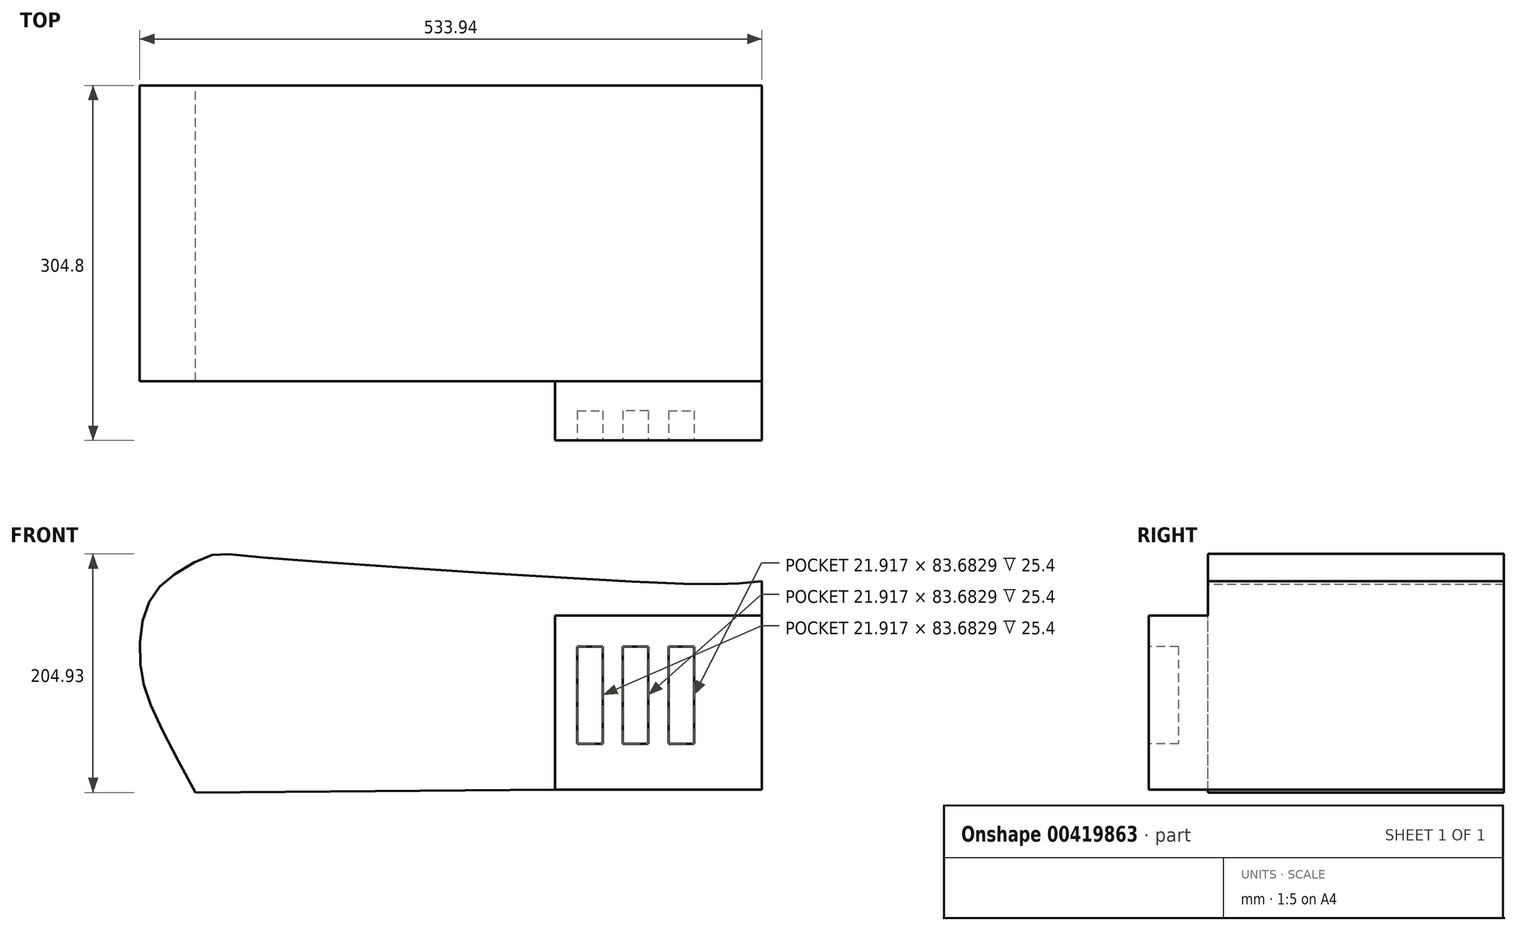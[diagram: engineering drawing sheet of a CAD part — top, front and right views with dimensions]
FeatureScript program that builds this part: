
annotation { "Feature Type Name" : "Feature", "Feature Type Description" : "" }
export const myFeature = defineFeature(function(context is Context, id is Id, definition is map)
    precondition{}
    {
        {
            var Q0;
            Q0=qCreatedBy(makeId("Front.planeOp"),FACE);
            var sketch = newSketch(context, id + "F0", { "sketchPlane" : qUnion([Q0])});
            skLineSegment(sketch, "E0.bottom", {"start": v(85.88, -146.83) * mm, "end": v(263.47, -146.83) * mm});
            skLineSegment(sketch, "E0.top", {"start": v(85.88, 2.72) * mm, "end": v(263.47, 2.72) * mm});
            skLineSegment(sketch, "E0.left", {"start": v(85.88, -146.83) * mm, "end": v(85.88, 2.72) * mm});
            skLineSegment(sketch, "E0.right", {"start": v(263.47, -146.83) * mm, "end": v(263.47, 2.72) * mm});
            skFitSpline(sketch, "E1", {"points": [v(-222.57, -149.17) * mm, v(-259.96, -76.73) * mm, v(-269.3, -44.02) * mm, v(-269.3, -8.96) * mm, v(-259.96, 19.08) * mm, v(-241.26, 37.77) * mm, v(-210.89, 54.13) * mm, v(-180.5, 54.13) * mm, v(179.35, 30.76) * mm, v(247.1, 30.76) * mm, v(286.83, 35.43) * mm, v(314.87, 40.1) * mm], "startDerivative": vector(-395.83, 720.92) * mm, "endDerivative": vector(404.96, 72.08) * mm});
            skLineSegment(sketch, "E2", {"start": v(-222.57, -149.17) * mm, "end": v(85.88, -146.83) * mm});
            skLineSegment(sketch, "E3", {"start": v(263.47, 2.72) * mm, "end": v(263.47, 32.4) * mm});
            skSolve(sketch);
        }
        {
            var Q0;
            Q0=makeQuery(id+"F0.imprint","IMPRINT",FACE,{"disambiguationData":[TD([[makeQuery(id+"F0.imprint","IMPRINT",EDGE,{"derivedFrom":sQuery(id+"F0.wireOp",EDGE,"E0.bottom")}),1.0]])]});
            extrude(context, id + "F1", {"entities" : qUnion([Q0]), "depth" : 304.8 * mm});
        }
        {
            var Q0;
            Q0 = qSketchRegion(id + "F0", true);
            extrude(context, id + "F2", {"entities" : qUnion([Q0]), "operationType" : NewBodyOperationType.ADD, "depth" : 254 * mm});
        }
        {
            var Q0;
            Q0=makeQuery(id+"F1.opExtrude","CAP_FACE",FACE,{"disambiguationData":[OSD([sQuery(id+"F0.wireOp",EDGE,"E0.bottom"),sQuery(id+"F0.wireOp",EDGE,"E0.top"),sQuery(id+"F0.wireOp",EDGE,"E0.left"),sQuery(id+"F0.wireOp",EDGE,"E0.right")])],"isStart":false});
            var sketch = newSketch(context, id + "F3", { "sketchPlane" : qUnion([Q0])});
            skLineSegment(sketch, "E4.bottom", {"start": v(105.11, -23.73) * mm, "end": v(127.03, -23.73) * mm});
            skLineSegment(sketch, "E4.top", {"start": v(105.11, -107.4) * mm, "end": v(127.03, -107.4) * mm});
            skLineSegment(sketch, "E4.left", {"start": v(105.11, -23.73) * mm, "end": v(105.11, -107.4) * mm});
            skLineSegment(sketch, "E4.right", {"start": v(127.03, -23.73) * mm, "end": v(127.03, -107.4) * mm});
            skLineSegment(sketch, "E5.MirrorCS", {"start": v(144.1, -23.73) * mm, "end": v(144.1, -107.4) * mm});
            skLineSegment(sketch, "E6.MirrorCS", {"start": v(166.02, -23.73) * mm, "end": v(166.02, -107.4) * mm});
            skLineSegment(sketch, "E7.MirrorCS", {"start": v(166.02, -23.73) * mm, "end": v(144.1, -23.73) * mm});
            skLineSegment(sketch, "E8.MirrorCS", {"start": v(166.02, -107.4) * mm, "end": v(144.1, -107.4) * mm});
            skPoint(sketch, "E9.startSnap0", {"position": v(174.67, 2.72) * mm});
            skPoint(sketch, "E9.endSnap0", {"position": v(174.67, -146.83) * mm});
            skLineSegment(sketch, "E10.MirrorCS", {"start": v(183.32, -23.73) * mm, "end": v(183.32, -107.4) * mm});
            skLineSegment(sketch, "E11.MirrorCS", {"start": v(205.24, -23.73) * mm, "end": v(205.24, -107.4) * mm});
            skLineSegment(sketch, "E12.MirrorCS", {"start": v(183.32, -23.73) * mm, "end": v(205.24, -23.73) * mm});
            skLineSegment(sketch, "E13.MirrorCS", {"start": v(183.32, -107.4) * mm, "end": v(205.24, -107.4) * mm});
            skPoint(sketch, "E14.orphan", {"position": v(174.67, 56.11) * mm});
            skPoint(sketch, "E9.end.orphan", {"position": v(174.67, -167.04) * mm});
            skLineSegment(sketch, "E15", {"start": v(85.88, -14.48) * mm, "end": v(-270.9, -14.48) * mm});
            skLineSegment(sketch, "E16", {"start": v(85.88, -72.06) * mm, "end": v(-260.65, -72.06) * mm});
            skLineSegment(sketch, "E17", {"start": v(-208.27, -148.82) * mm, "end": v(-208.27, 53.84) * mm});
            skLineSegment(sketch, "E18", {"start": v(-126.3, -146.55) * mm, "end": v(-126.3, 51.56) * mm});
            skLineSegment(sketch, "E19.MirrorCS", {"start": v(-44.32, -148.82) * mm, "end": v(-44.32, 53.84) * mm});
            skLineSegment(sketch, "E20.MirrorCS", {"start": v(37.65, -146.55) * mm, "end": v(37.65, 51.56) * mm});
            skLineSegment(sketch, "E21", {"start": v(121.9, 2.72) * mm, "end": v(121.9, 36.76) * mm});
            skLineSegment(sketch, "E22", {"start": v(194.77, 2.72) * mm, "end": v(194.77, 31.07) * mm});
            skFitSpline(sketch, "E23.0", {"points": [v(-228.14, -152.22) * mm, v(-231.8, -145.55) * mm, v(-239.14, -132.18) * mm, v(-249.57, -112.77) * mm, v(-257.28, -97.7) * mm, v(-262.56, -86.6) * mm, v(-266.01, -78.84) * mm, v(-268.88, -71.7) * mm, v(-271.21, -64.98) * mm, v(-273.07, -58.5) * mm, v(-274.26, -53.16) * mm, v(-275.03, -48.85) * mm, v(-275.52, -45.57) * mm, v(-275.93, -42.23) * mm, v(-276.39, -37.68) * mm, v(-276.76, -31.84) * mm, v(-276.87, -24.7) * mm, v(-276.62, -17.51) * mm, v(-275.97, -10.37) * mm, v(-274.9, -3.37) * mm, v(-273.36, 3.4) * mm, v(-271.36, 9.88) * mm, v(-269.3, 15) * mm, v(-267.38, 18.9) * mm, v(-265.81, 21.72) * mm, v(-264.1, 24.42) * mm, v(-261.67, 27.84) * mm, v(-258.3, 31.82) * mm, v(-253.73, 36.2) * mm, v(-249.5, 39.63) * mm, v(-245.85, 42.32) * mm, v(-242.97, 44.32) * mm, v(-239.96, 46.33) * mm, v(-235.8, 48.95) * mm, v(-230.43, 52.12) * mm, v(-225.05, 54.97) * mm, v(-220.85, 56.99) * mm, v(-217.78, 58.34) * mm, v(-215.3, 59.31) * mm, v(-213.38, 60) * mm, v(-211.5, 60.6) * mm, v(-209.18, 61.23) * mm, v(-206.4, 61.76) * mm, v(-203.59, 62.05) * mm, v(-200.73, 62.14) * mm, v(-197.74, 62.06) * mm, v(-194.52, 61.84) * mm, v(-190.94, 61.53) * mm, v(-186.86, 61.13) * mm, v(-182.95, 60.74) * mm, v(-179.44, 60.4) * mm, v(-175.66, 60.05) * mm, v(-170.44, 59.59) * mm, v(-163.43, 59) * mm, v(-155.71, 58.36) * mm, v(-144.54, 57.47) * mm, v(-129.05, 56.3) * mm, v(-108.37, 54.77) * mm, v(-85.96, 53.18) * mm, v(-54.25, 50.99) * mm, v(-12.06, 48.18) * mm, v(31.14, 45.43) * mm, v(64.88, 43.36) * mm, v(89.42, 41.9) * mm, v(112.84, 40.55) * mm, v(134.77, 39.33) * mm, v(151.53, 38.45) * mm, v(163.83, 37.84) * mm, v(172.46, 37.42) * mm, v(180.46, 37.06) * mm, v(187.77, 36.76) * mm, v(194.46, 36.5) * mm, v(202.61, 36.23) * mm, v(211.5, 36) * mm, v(220.51, 35.93) * mm, v(228.27, 36.03) * mm, v(234.05, 36.24) * mm, v(238.5, 36.49) * mm, v(241.8, 36.7) * mm, v(245.12, 36.96) * mm, v(248.52, 37.25) * mm, v(252, 37.57) * mm, v(256.73, 38.04) * mm, v(260.34, 38.43) * mm, v(262.75, 38.7) * mm]});
            skSolve(sketch);
        }
        {
            var Q0;
            Q0=makeQuery(id+"F3.imprint","IMPRINT",FACE,{"disambiguationData":[TD([[makeQuery(id+"F3.imprint","IMPRINT",EDGE,{"derivedFrom":sQuery(id+"F3.wireOp",EDGE,"E4.bottom")}),-1.0]])]});
            var Q1;
            Q1=makeQuery(id+"F3.imprint","IMPRINT",FACE,{"disambiguationData":[TD([[makeQuery(id+"F3.imprint","IMPRINT",EDGE,{"derivedFrom":sQuery(id+"F3.wireOp",EDGE,"E5.MirrorCS")}),1.0]])]});
            var Q2;
            Q2=makeQuery(id+"F3.imprint","IMPRINT",FACE,{"disambiguationData":[TD([[makeQuery(id+"F3.imprint","IMPRINT",EDGE,{"derivedFrom":sQuery(id+"F3.wireOp",EDGE,"E10.MirrorCS")}),1.0]])]});
            extrude(context, id + "F4", {"entities" : qUnion([Q0, Q1, Q2]), "operationType" : NewBodyOperationType.REMOVE, "oppositeDirection" : true, "depth" : 25.4 * mm});
        }
    });
